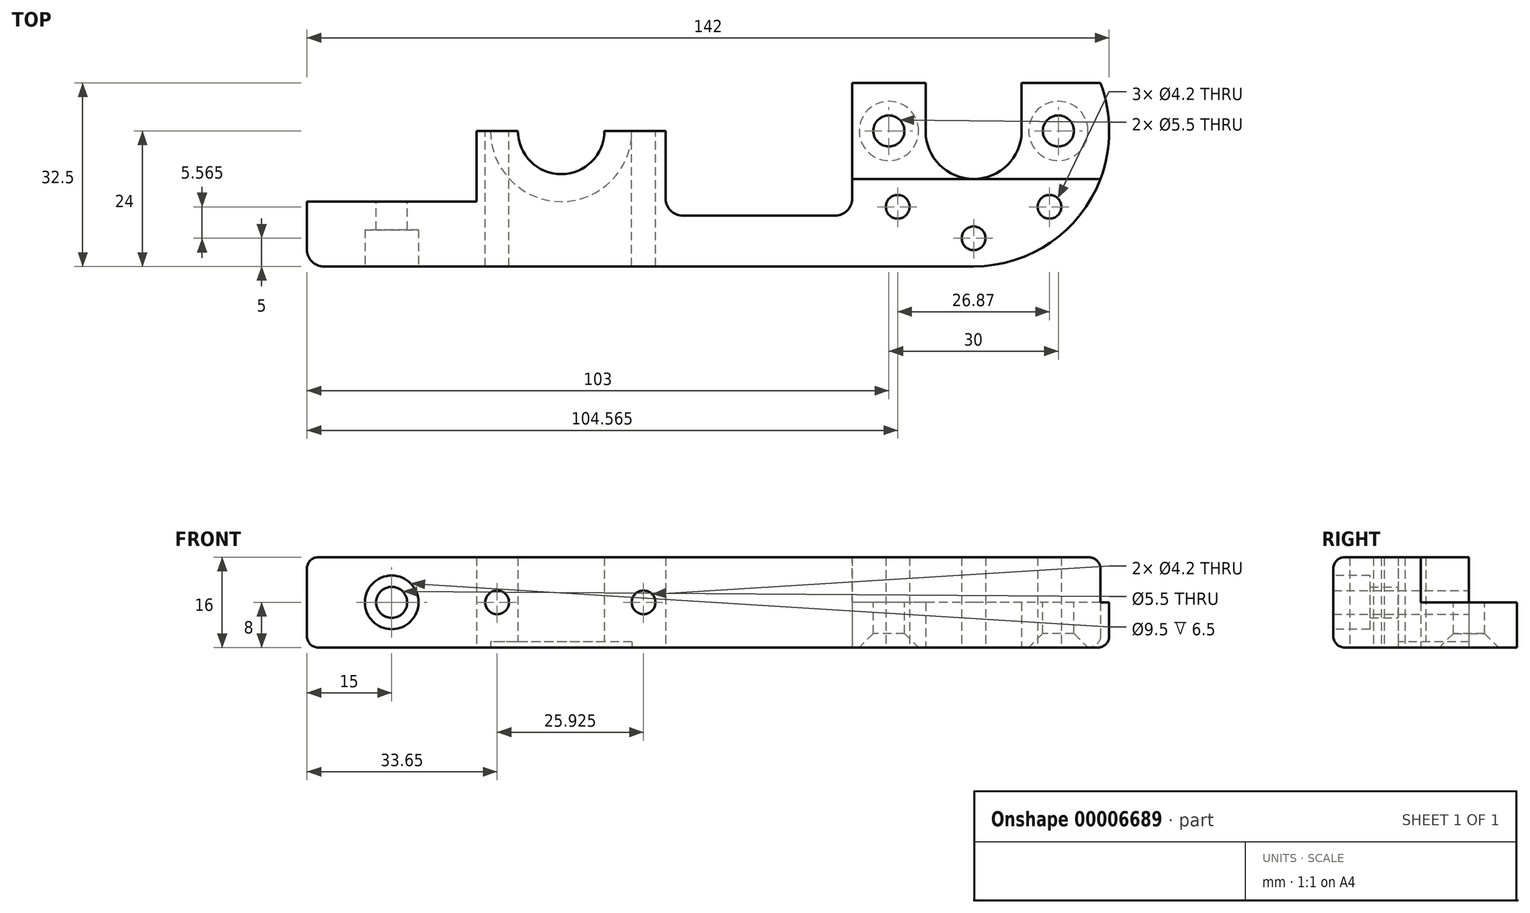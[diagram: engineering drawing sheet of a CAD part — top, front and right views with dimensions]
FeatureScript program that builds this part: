
annotation { "Feature Type Name" : "Feature", "Feature Type Description" : "" }
export const myFeature = defineFeature(function(context is Context, id is Id, definition is map)
    precondition{}
    {
        {
            var Q0;
            Q0=qCreatedBy(makeId("Top.planeOp"),FACE);
            var sketch = newSketch(context, id + "F0", { "sketchPlane" : qUnion([Q0])});
            skLineSegment(sketch, "E0", {"start": v(30, 20.5) * mm, "end": v(30, 8) * mm});
            skLineSegment(sketch, "E1", {"start": v(30, 8) * mm, "end": v(0, 8) * mm});
            skArc(sketch, "E2", {"start": v(37.35, 20.5) * mm, "mid": v(45, 12.85) * mm, "end": v(52.65, 20.5) * mm});
            skArc(sketch, "E3", {"start": v(109.5, 20.5) * mm, "mid": v(118, 12) * mm, "end": v(126.5, 20.5) * mm});
            skLineSegment(sketch, "E4.top", {"start": v(63.5, 5.5) * mm, "end": v(96.5, 5.5) * mm});
            skLineSegment(sketch, "E4.right", {"start": v(96.5, 29) * mm, "end": v(96.5, 5.5) * mm});
            skLineSegment(sketch, "E5.0", {"start": v(118, -3.5) * mm, "end": v(0, -3.5) * mm});
            skArc(sketch, "E6.trimOffspring", {"start": v(118, -3.5) * mm, "mid": v(137.75, 6.86) * mm, "end": v(140.44, 29) * mm});
            skLineSegment(sketch, "E7", {"start": v(0, 8) * mm, "end": v(0, -3.5) * mm});
            skPoint(sketch, "E8.center", {"position": v(0, 0) * mm});
            skCircle(sketch, "E9.3.0", {"center": v(104.56, 7.06) * mm, "radius": 2.1 * mm});
            skCircle(sketch, "E9.4.0", {"center": v(118, 1.5) * mm, "radius": 2.1 * mm});
            skCircle(sketch, "E9.5.0", {"center": v(131.44, 7.06) * mm, "radius": 2.1 * mm});
            skLineSegment(sketch, "E10", {"start": v(30, 20.5) * mm, "end": v(37.35, 20.5) * mm});
            skLineSegment(sketch, "E11", {"start": v(96.5, 29) * mm, "end": v(109.5, 29) * mm});
            skLineSegment(sketch, "E12.0", {"start": v(126.5, 20.5) * mm, "end": v(126.5, 29) * mm});
            skLineSegment(sketch, "E13.0", {"start": v(109.5, 20.5) * mm, "end": v(109.5, 29) * mm});
            skLineSegment(sketch, "E14.trimOffspring", {"start": v(126.5, 29) * mm, "end": v(140.44, 29) * mm});
            skLineSegment(sketch, "E15.trimOffspring", {"start": v(52.65, 20.5) * mm, "end": v(63.5, 20.5) * mm});
            skLineSegment(sketch, "E16.0", {"start": v(63.5, 20.5) * mm, "end": v(63.5, 5.5) * mm});
            skSolve(sketch);
        }
        {
            var Q0;
            Q0=makeQuery(id+"F0.imprint","IMPRINT",FACE,{"disambiguationData":[TD([[makeQuery(id+"F0.imprint","IMPRINT",EDGE,{"derivedFrom":sQuery(id+"F0.wireOp",EDGE,"E0")}),1.0]])]});
            extrude(context, id + "F1", {"entities" : qUnion([Q0]), "depth" : 16 * mm});
        }
        {
            var Q0;
            Q0=makeQuery(id+"F1.opExtrude","SWEPT_FACE",FACE,{"disambiguationData":[OSD([sQuery(id+"F0.wireOp",EDGE,"E4.right")])]});
            var sketch = newSketch(context, id + "F2", { "sketchPlane" : qUnion([Q0])});
            skLineSegment(sketch, "E17.top", {"start": v(-29, 16) * mm, "end": v(-12, 16) * mm});
            skLineSegment(sketch, "E17.left", {"start": v(-29, 8) * mm, "end": v(-29, 16) * mm});
            skLineSegment(sketch, "E18", {"start": v(-29, 8) * mm, "end": v(-12, 8) * mm});
            skPoint(sketch, "E17.bottom.end.orphan", {"position": v(-20.5, 0) * mm});
            skLineSegment(sketch, "E19.0", {"start": v(-12, 8) * mm, "end": v(-12, 16) * mm});
            skPoint(sketch, "E20.orphan", {"position": v(-20.5, 16) * mm});
            skSolve(sketch);
        }
        {
            var Q0;
            Q0=qSketchRegion(id+"F2",true);
            extrude(context, id + "F3", {"entities" : qUnion([Q0]), "operationType" : NewBodyOperationType.REMOVE, "endBound" : BoundingType.THROUGH_ALL, "oppositeDirection" : true, "depth" : 25 * mm});
        }
        {
            var Q0;
            Q0=makeQuery(id+"F1.opExtrude","SWEPT_FACE",FACE,{"disambiguationData":[OSD([sQuery(id+"F0.wireOp",EDGE,"E15.trimOffspring")])]});
            var sketch = newSketch(context, id + "F4", { "sketchPlane" : qUnion([Q0])});
            skCircle(sketch, "E21", {"center": v(-59.58, 8) * mm, "radius": 2.1 * mm});
            skCircle(sketch, "E22", {"center": v(-33.65, 8) * mm, "radius": 2.1 * mm});
            skCircle(sketch, "E23", {"center": v(-15, 8) * mm, "radius": 2.75 * mm});
            skSolve(sketch);
        }
        {
            var Q0;
            Q0=qSketchRegion(id+"F4",true);
            extrude(context, id + "F5", {"entities" : qUnion([Q0]), "operationType" : NewBodyOperationType.REMOVE, "endBound" : BoundingType.THROUGH_ALL, "oppositeDirection" : true, "depth" : 25 * mm});
        }
        {
            var Q0;
            Q0=makeQuery(id+"F1.opExtrude","SWEPT_EDGE",EDGE,{"disambiguationData":[OSD([sQuery(id+"F0.wireOp",EDGE,"E4.top"),sQuery(id+"F0.wireOp",EDGE,"E4.right")])]});
            var Q1;
            Q1=makeQuery(id+"F1.opExtrude","SWEPT_EDGE",EDGE,{"disambiguationData":[OSD([sQuery(id+"F0.wireOp",EDGE,"E4.top"),sQuery(id+"F0.wireOp",EDGE,"E4.left")])]});
            var Q2;
            Q2=makeQuery(id+"F1.opExtrude","SWEPT_EDGE",EDGE,{"disambiguationData":[OSD([sQuery(id+"F0.wireOp",EDGE,"E5.0"),sQuery(id+"F0.wireOp",EDGE,"E7")])]});
            fillet(context, id + "F6", {"entities" : qUnion([Q0, Q1, Q2]), "radius" : 3 * mm, "tangentPropagation" : true, "allowEdgeOverflow" : false});
        }
        {
            var Q0;
            {var subQ0=makeQuery(id+"F3.opExtrude","SWEPT_FACE",FACE,{"disambiguationData":[OSD([sQuery(id+"F2.wireOp",EDGE,"E18")])]});Q0=makeQuery(id+"F3.boolean.opBoolean","COPY",FACE,{"disambiguationData":[TD([makeQuery(id+"F1.opExtrude","SWEPT_FACE",FACE,{"disambiguationData":[OSD([sQuery(id+"F0.wireOp",EDGE,"E6.trimOffspring")])]})])],"derivedFrom":subQ0});}
            var sketch = newSketch(context, id + "F7", { "sketchPlane" : qUnion([Q0])});
            skLineSegment(sketch, "E24", {"start": v(126.5, 29) * mm, "end": v(126.5, 12) * mm, "construction": true});
            skLineSegment(sketch, "E25.0", {"start": v(103, 29) * mm, "end": v(103, 12) * mm, "construction": true});
            skLineSegment(sketch, "E26.0", {"start": v(133, 29) * mm, "end": v(133, 12) * mm, "construction": true});
            skLineSegment(sketch, "E27", {"start": v(133, 20.5) * mm, "end": v(103, 20.5) * mm, "construction": true});
            skCircle(sketch, "E28", {"center": v(133, 20.5) * mm, "radius": 2.75 * mm});
            skCircle(sketch, "E29", {"center": v(103, 20.5) * mm, "radius": 2.75 * mm});
            skSolve(sketch);
        }
        {
            var Q0;
            Q0=qSketchRegion(id+"F7",true);
            extrude(context, id + "F8", {"entities" : qUnion([Q0]), "operationType" : NewBodyOperationType.REMOVE, "endBound" : BoundingType.THROUGH_ALL, "oppositeDirection" : true, "depth" : 25 * mm});
        }
        {
            var Q0;
            Q0=makeQuery(id+"F1.opExtrude","CAP_EDGE",EDGE,{"disambiguationData":[OSD([sQuery(id+"F0.wireOp",EDGE,"E7")])],"isStart":false});
            var Q1;
            Q1=makeQuery(id+"F1.opExtrude","CAP_EDGE",EDGE,{"disambiguationData":[OSD([sQuery(id+"F0.wireOp",EDGE,"E7")])],"isStart":true});
            fillet(context, id + "F9", {"entities" : qUnion([Q0, Q1]), "radius" : 2 * mm, "tangentPropagation" : true, "allowEdgeOverflow" : false});
        }
        {
            var Q0;
            Q0=makeQuery(id+"F1.opExtrude","CAP_FACE",FACE,{"disambiguationData":[OSD([sQuery(id+"F0.wireOp",EDGE,"E0"),sQuery(id+"F0.wireOp",EDGE,"E1"),sQuery(id+"F0.wireOp",EDGE,"E2"),sQuery(id+"F0.wireOp",EDGE,"E3"),sQuery(id+"F0.wireOp",EDGE,"E4.top"),sQuery(id+"F0.wireOp",EDGE,"E4.left"),sQuery(id+"F0.wireOp",EDGE,"E4.right"),sQuery(id+"F0.wireOp",EDGE,"E5.0"),sQuery(id+"F0.wireOp",EDGE,"E6.trimOffspring"),sQuery(id+"F0.wireOp",EDGE,"E7"),sQuery(id+"F0.wireOp",EDGE,"E9.3.0"),sQuery(id+"F0.wireOp",EDGE,"E9.4.0"),sQuery(id+"F0.wireOp",EDGE,"E9.5.0"),sQuery(id+"F0.wireOp",EDGE,"E10"),sQuery(id+"F0.wireOp",EDGE,"E11"),sQuery(id+"F0.wireOp",EDGE,"E12.0"),sQuery(id+"F0.wireOp",EDGE,"E13.0"),sQuery(id+"F0.wireOp",EDGE,"E14.trimOffspring"),sQuery(id+"F0.wireOp",EDGE,"E15.trimOffspring")])],"isStart":true});
            var sketch = newSketch(context, id + "F10", { "sketchPlane" : qUnion([Q0])});
            skCircle(sketch, "E30", {"center": v(45, -20.5) * mm, "radius": 12.5 * mm});
            skSolve(sketch);
        }
        {
            var Q0;
            Q0 = qSketchRegion(id + "F10", true);
            extrude(context, id + "F11", {"entities" : qUnion([Q0]), "operationType" : NewBodyOperationType.REMOVE, "oppositeDirection" : true, "depth" : 1 * mm});
        }
        {
            var Q0;
            Q0=makeQuery(id+"F8.boolean.opBoolean","INTERSECT",EDGE,{"derivedFrom":[makeQuery(id+"F1.opExtrude","CAP_FACE",FACE,{"disambiguationData":[OSD([sQuery(id+"F0.wireOp",EDGE,"E0"),sQuery(id+"F0.wireOp",EDGE,"E1"),sQuery(id+"F0.wireOp",EDGE,"E2"),sQuery(id+"F0.wireOp",EDGE,"E3"),sQuery(id+"F0.wireOp",EDGE,"E4.top"),sQuery(id+"F0.wireOp",EDGE,"E4.left"),sQuery(id+"F0.wireOp",EDGE,"E4.right"),sQuery(id+"F0.wireOp",EDGE,"E5.0"),sQuery(id+"F0.wireOp",EDGE,"E6.trimOffspring"),sQuery(id+"F0.wireOp",EDGE,"E7"),sQuery(id+"F0.wireOp",EDGE,"E9.3.0"),sQuery(id+"F0.wireOp",EDGE,"E9.4.0"),sQuery(id+"F0.wireOp",EDGE,"E9.5.0"),sQuery(id+"F0.wireOp",EDGE,"E10"),sQuery(id+"F0.wireOp",EDGE,"E11"),sQuery(id+"F0.wireOp",EDGE,"E12.0"),sQuery(id+"F0.wireOp",EDGE,"E13.0"),sQuery(id+"F0.wireOp",EDGE,"E14.trimOffspring"),sQuery(id+"F0.wireOp",EDGE,"E15.trimOffspring")])],"isStart":true}),makeQuery(id+"F8.opExtrude","SWEPT_FACE",FACE,{"disambiguationData":[OSD([sQuery(id+"F7.wireOp",EDGE,"E29")])]})]});
            var Q1;
            Q1=makeQuery(id+"F8.boolean.opBoolean","INTERSECT",EDGE,{"derivedFrom":[makeQuery(id+"F1.opExtrude","CAP_FACE",FACE,{"disambiguationData":[OSD([sQuery(id+"F0.wireOp",EDGE,"E0"),sQuery(id+"F0.wireOp",EDGE,"E1"),sQuery(id+"F0.wireOp",EDGE,"E2"),sQuery(id+"F0.wireOp",EDGE,"E3"),sQuery(id+"F0.wireOp",EDGE,"E4.top"),sQuery(id+"F0.wireOp",EDGE,"E4.left"),sQuery(id+"F0.wireOp",EDGE,"E4.right"),sQuery(id+"F0.wireOp",EDGE,"E5.0"),sQuery(id+"F0.wireOp",EDGE,"E6.trimOffspring"),sQuery(id+"F0.wireOp",EDGE,"E7"),sQuery(id+"F0.wireOp",EDGE,"E9.3.0"),sQuery(id+"F0.wireOp",EDGE,"E9.4.0"),sQuery(id+"F0.wireOp",EDGE,"E9.5.0"),sQuery(id+"F0.wireOp",EDGE,"E10"),sQuery(id+"F0.wireOp",EDGE,"E11"),sQuery(id+"F0.wireOp",EDGE,"E12.0"),sQuery(id+"F0.wireOp",EDGE,"E13.0"),sQuery(id+"F0.wireOp",EDGE,"E14.trimOffspring"),sQuery(id+"F0.wireOp",EDGE,"E15.trimOffspring")])],"isStart":true}),makeQuery(id+"F8.opExtrude","SWEPT_FACE",FACE,{"disambiguationData":[OSD([sQuery(id+"F7.wireOp",EDGE,"E28")])]})]});
            chamfer(context, id + "F12", {"entities" : qUnion([Q0, Q1]), "width" : 2.5 * mm, "tangentPropagation" : true});
        }
        {
            var Q0;
            Q0=makeQuery(id+"F1.opExtrude","SWEPT_FACE",FACE,{"disambiguationData":[OSD([sQuery(id+"F0.wireOp",EDGE,"E5.0")])]});
            var sketch = newSketch(context, id + "F13", { "sketchPlane" : qUnion([Q0])});
            skCircle(sketch, "E31", {"center": v(15, 8) * mm, "radius": 4.75 * mm});
            skSolve(sketch);
        }
        {
            var Q0;
            Q0 = qSketchRegion(id + "F13", true);
            extrude(context, id + "F14", {"entities" : qUnion([Q0]), "operationType" : NewBodyOperationType.REMOVE, "oppositeDirection" : true, "depth" : 6.5 * mm});
        }
    });
